# Revit family: 63_UN_HighBay_Coreline Highbay BY122X G5 250-300_Signify
name_source: partatom
category: Lighting Fixtures
units: mm (PartAtom-declared; Revit-internal decimal feet)

## family parameters
Always vertical = No
Cut with Voids When Loaded = No
Light Source = Yes
OmniClass Number = 23.80.70.11.14.11
OmniClass Title = Downlights
Part Type = Normal
Room Calculation Point = Yes
Round Connector Dimension = Use Diameter
Shared = No
Work Plane-Based = No

## types (2) — shared parameters
Apparent Load = 166 VA
Assembly Code = 63.0
Color Filter = 16777215
Dimming Lamp Color Temperature Shift = <None>
Emit Shape Visible in Rendering = No
Emit from Circle Diameter = 317 mm  [stored 1.04003 ft]
Housing_Material = Rubber, Black
IfcExportAs = IfcLightFixtureType
IfcExportType = USERDEFINED
Lamp = LED
Manufacturer = Signify
Model = Coreline Highbay Gen5
Tilt Angle = 90.00°
Type Comments = 250-300
URL = https://www.signify.com
Voltage = 230 V
Wattage Comments = 166 W

## per-type parameters (varying)
| type | Photometric Web File |
| BY122X G5 LED200S_840 NB SIA H4 | BY122X G5 LED200S_840 NB SIA H4.ies |
| BY122X G5 LED250S_840 WB SIA H4 | BY122X G5 LED250S_840 WB SIA H4.ies |

note: [stored X ft] marks values corroborated as IEEE doubles in the binary element streams (Revit-internal decimal feet)

## geometry (parser evidence)
native form markers: Sweep x4
no freeform markers — native parametric forms only
